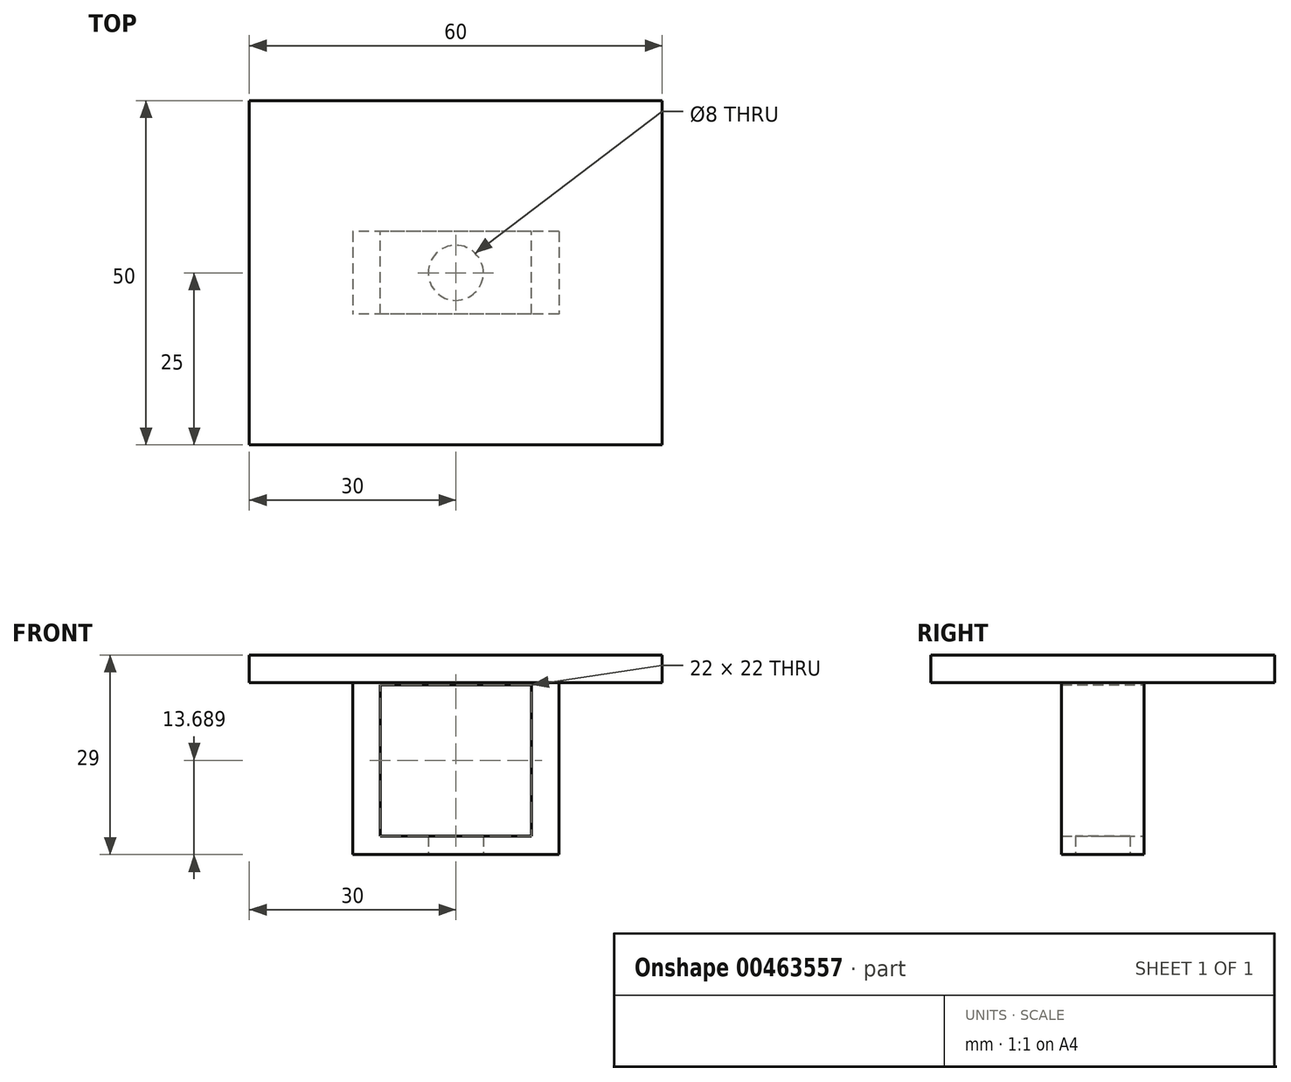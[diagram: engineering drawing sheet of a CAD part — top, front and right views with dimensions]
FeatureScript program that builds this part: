
annotation { "Feature Type Name" : "Feature", "Feature Type Description" : "" }
export const myFeature = defineFeature(function(context is Context, id is Id, definition is map)
    precondition{}
    {
        {
            var Q0;
            Q0=qCreatedBy(makeId("Front.planeOp"),FACE);
            var sketch = newSketch(context, id + "F0", { "sketchPlane" : qUnion([Q0])});
            skLineSegment(sketch, "E0.bottom", {"start": v(30, 2) * mm, "end": v(-30, 2) * mm});
            skLineSegment(sketch, "E0.top", {"start": v(30, -2) * mm, "end": v(-30, -2) * mm});
            skLineSegment(sketch, "E0.left", {"start": v(30, 2) * mm, "end": v(30, -2) * mm});
            skLineSegment(sketch, "E0.right", {"start": v(-30, 2) * mm, "end": v(-30, -2) * mm});
            skPoint(sketch, "E0.middle", {"position": v(0, 0) * mm});
            skSolve(sketch);
        }
        {
            var Q0;
            Q0 = qSketchRegion(id + "F0", true);
            extrude(context, id + "F1", {"entities" : qUnion([Q0]), "depth" : 25 * mm, "offsetDistance" : 25 * mm, "hasSecondDirection" : true, "secondDirectionOppositeDirection" : true, "secondDirectionDepth" : 25 * mm});
        }
        {
            var Q0;
            Q0=makeQuery(id+"F1.opExtrude","SWEPT_FACE",FACE,{"disambiguationData":[OSD([sQuery(id+"F0.wireOp",EDGE,"E0.top")])]});
            var sketch = newSketch(context, id + "F2", { "sketchPlane" : qUnion([Q0])});
            skLineSegment(sketch, "E1.bottom", {"start": v(15, -6) * mm, "end": v(-15, -6) * mm});
            skLineSegment(sketch, "E1.top", {"start": v(15, 6) * mm, "end": v(-15, 6) * mm});
            skLineSegment(sketch, "E1.left", {"start": v(15, -6) * mm, "end": v(15, 6) * mm});
            skLineSegment(sketch, "E1.right", {"start": v(-15, -6) * mm, "end": v(-15, 6) * mm});
            skPoint(sketch, "E1.middle", {"position": v(0, 0) * mm});
            skSolve(sketch);
        }
        {
            var Q0;
            Q0 = qSketchRegion(id + "F2", true);
            extrude(context, id + "F3", {"entities" : qUnion([Q0]), "operationType" : NewBodyOperationType.ADD, "depth" : 25 * mm, "offsetDistance" : 25 * mm});
        }
        {
            var Q0;
            Q0=makeQuery(id+"F3.opExtrude","SWEPT_FACE",FACE,{"disambiguationData":[OSD([sQuery(id+"F2.wireOp",EDGE,"E1.bottom")])]});
            var sketch = newSketch(context, id + "F4", { "sketchPlane" : qUnion([Q0])});
            skLineSegment(sketch, "E2.bottom", {"start": v(-11, -24.31) * mm, "end": v(11, -24.31) * mm});
            skLineSegment(sketch, "E2.top", {"start": v(-11, -2.31) * mm, "end": v(11, -2.31) * mm});
            skLineSegment(sketch, "E2.left", {"start": v(-11, -24.31) * mm, "end": v(-11, -2.31) * mm});
            skLineSegment(sketch, "E2.right", {"start": v(11, -24.31) * mm, "end": v(11, -2.31) * mm});
            skPoint(sketch, "E2.middle", {"position": v(0, -13.31) * mm});
            skPoint(sketch, "E2.middle.positionSnap0", {"position": v(0, -27) * mm});
            skPoint(sketch, "E2.centerSnap0", {"position": v(0, -27) * mm});
            skSolve(sketch);
        }
        {
            var Q0;
            Q0 = qSketchRegion(id + "F4", true);
            extrude(context, id + "F5", {"entities" : qUnion([Q0]), "operationType" : NewBodyOperationType.REMOVE, "oppositeDirection" : true, "depth" : 25 * mm, "offsetDistance" : 25 * mm});
        }
        {
            var Q0;
            Q0=makeQuery(id+"F3.opExtrude","CAP_FACE",FACE,{"disambiguationData":[OSD([sQuery(id+"F2.wireOp",EDGE,"E1.bottom"),sQuery(id+"F2.wireOp",EDGE,"E1.top"),sQuery(id+"F2.wireOp",EDGE,"E1.left"),sQuery(id+"F2.wireOp",EDGE,"E1.right")])],"isStart":false});
            var sketch = newSketch(context, id + "F6", { "sketchPlane" : qUnion([Q0])});
            skCircle(sketch, "E3", {"center": v(0, 0) * mm, "radius": 4 * mm});
            skSolve(sketch);
        }
        {
            var Q0;
            Q0=makeQuery(id+"F6.imprint","IMPRINT",FACE,{"disambiguationData":[TD([[makeQuery(id+"F6.imprint","IMPRINT",EDGE,{"derivedFrom":sQuery(id+"F6.wireOp",EDGE,"E3")}),1.0]])]});
            var Q1;
            Q1=sQuery(id+"F6.wireOp",EDGE,"E3");
            extrude(context, id + "F7", {"entities" : qUnion([Q0]), "operationType" : NewBodyOperationType.REMOVE, "surfaceEntities" : qUnion([Q1]), "oppositeDirection" : true, "depth" : 10 * mm, "offsetDistance" : 25 * mm});
        }
    });
